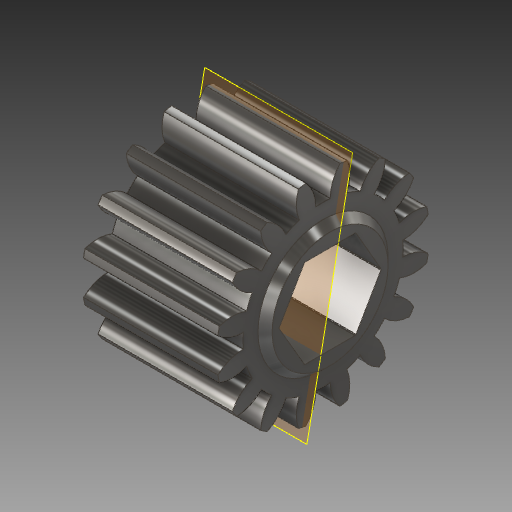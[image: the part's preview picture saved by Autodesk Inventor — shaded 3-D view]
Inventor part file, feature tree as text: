
AUTODESK INVENTOR PART (.ipt)
format: ipt  version: 2017.1 (Build 211199000, 199)  size: 313,344 bytes
history: native  units: in
note: dims shown in document units (in); Inventor stores cm internally (conversion verified against a paired STEP export)
features: plane x1, other x1
ambient origin geometry x8: Origin, YZ Plane, XZ Plane, XY Plane, X Axis, Y Axis, Z Axis, Center Point
bodies: Solid1 (feature_tree)
feature tree (2):
  plane  "Work Plane1"
  other  "Bore"
